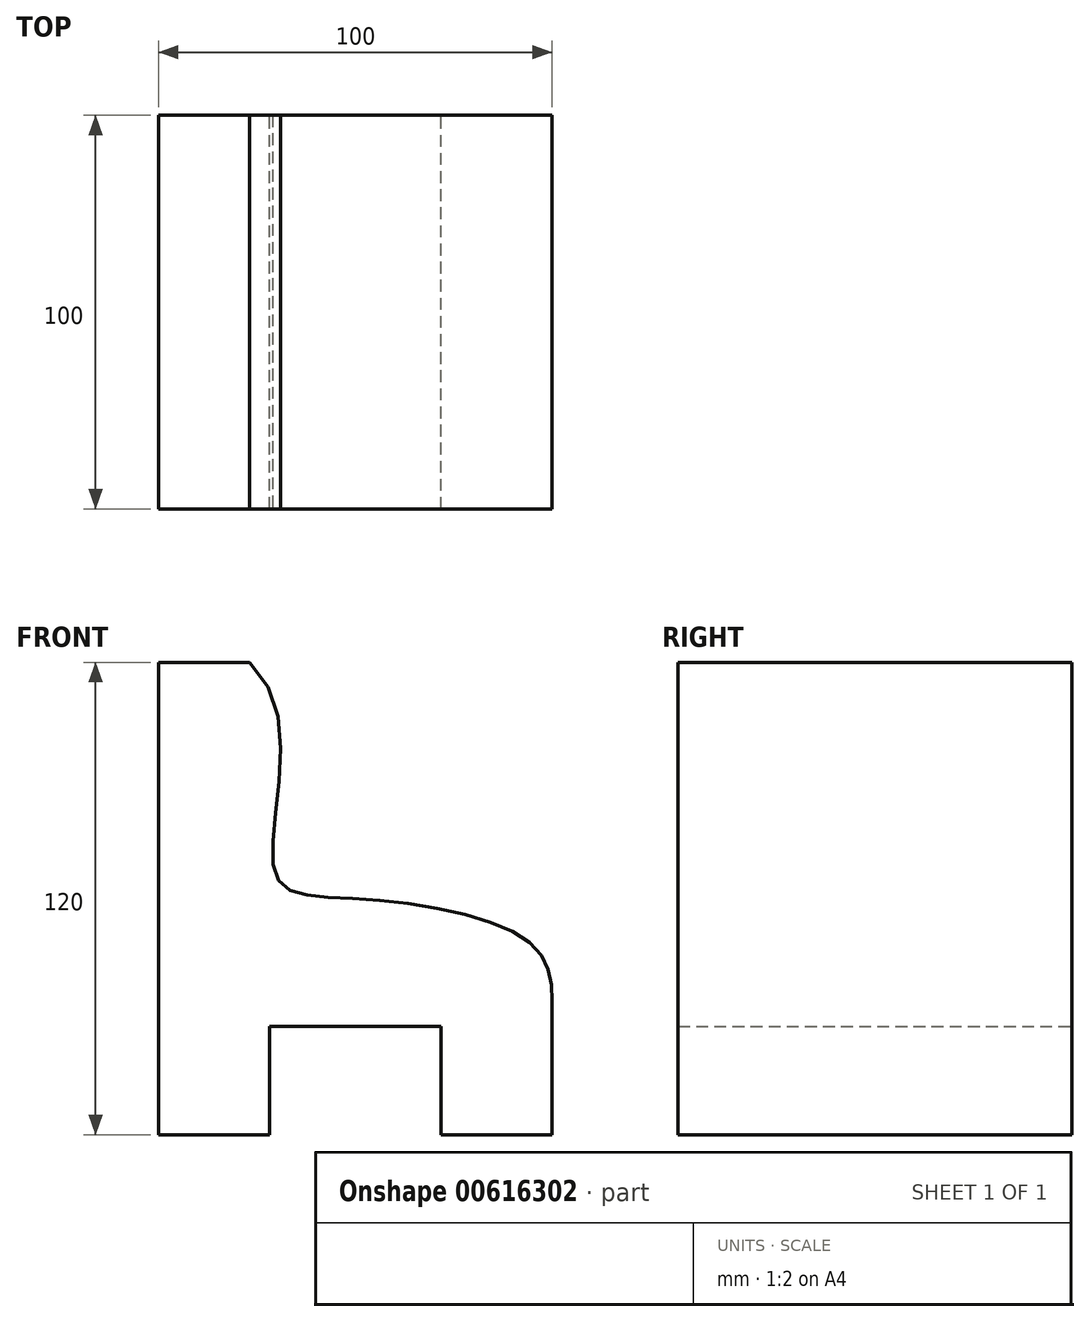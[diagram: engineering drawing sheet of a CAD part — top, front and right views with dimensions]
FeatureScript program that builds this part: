
annotation { "Feature Type Name" : "Feature", "Feature Type Description" : "" }
export const myFeature = defineFeature(function(context is Context, id is Id, definition is map)
    precondition{}
    {
        {
            var Q0;
            Q0=qCreatedBy(makeId("Front.planeOp"),FACE);
            var sketch = newSketch(context, id + "F0", { "sketchPlane" : qUnion([Q0])});
            skLineSegment(sketch, "E0.bottom", {"start": v(50, -60) * mm, "end": v(21.8, -60) * mm});
            skLineSegment(sketch, "E0.top", {"start": v(-26.88, 60) * mm, "end": v(-50, 60) * mm});
            skLineSegment(sketch, "E0.left", {"start": v(50, -60) * mm, "end": v(50, -26.03) * mm});
            skLineSegment(sketch, "E0.right", {"start": v(-50, -60) * mm, "end": v(-50, 60) * mm});
            skPoint(sketch, "E0.middle", {"position": v(0, 0) * mm});
            skFitSpline(sketch, "E1", {"points": [v(-26.88, 60) * mm, v(-20.54, 6.74) * mm, v(0, 0) * mm, v(44, -11) * mm, v(50, -26.03) * mm], "startDerivative": vector(141.16, -127.63) * mm, "endDerivative": vector(0, -96.77) * mm});
            skLineSegment(sketch, "E2.top", {"start": v(-21.8, -32.47) * mm, "end": v(21.8, -32.47) * mm});
            skLineSegment(sketch, "E2.left", {"start": v(-21.8, -60) * mm, "end": v(-21.8, -32.47) * mm});
            skLineSegment(sketch, "E2.right", {"start": v(21.8, -60) * mm, "end": v(21.8, -32.47) * mm});
            skPoint(sketch, "E2.middle", {"position": v(0, -46.23) * mm});
            skPoint(sketch, "E3.orphan", {"position": v(50, 60) * mm});
            skLineSegment(sketch, "E4.trimOffspring", {"start": v(-21.8, -60) * mm, "end": v(-50, -60) * mm});
            skSolve(sketch);
        }
        {
            var Q0;
            Q0=qCreatedBy(makeId("Top.planeOp"),FACE);
            var sketch = newSketch(context, id + "F1", { "sketchPlane" : qUnion([Q0])});
            skLineSegment(sketch, "E5", {"start": v(-30.48, 0) * mm, "end": v(-30.48, 100) * mm});
            skSolve(sketch);
        }
        {
            var Q0;
            Q0=makeQuery(id+"F0.imprint","IMPRINT",FACE,{"disambiguationData":[TD([[makeQuery(id+"F0.imprint","IMPRINT",EDGE,{"derivedFrom":sQuery(id+"F0.wireOp",EDGE,"E0.bottom")}),-1.0]])]});
            var Q1;
            Q1=sQuery(id+"F1.wireOp",EDGE,"E5");
            sweep(context, id + "F2", {"profiles" : qUnion([Q0]), "path" : qUnion([Q1])});
        }
    });
